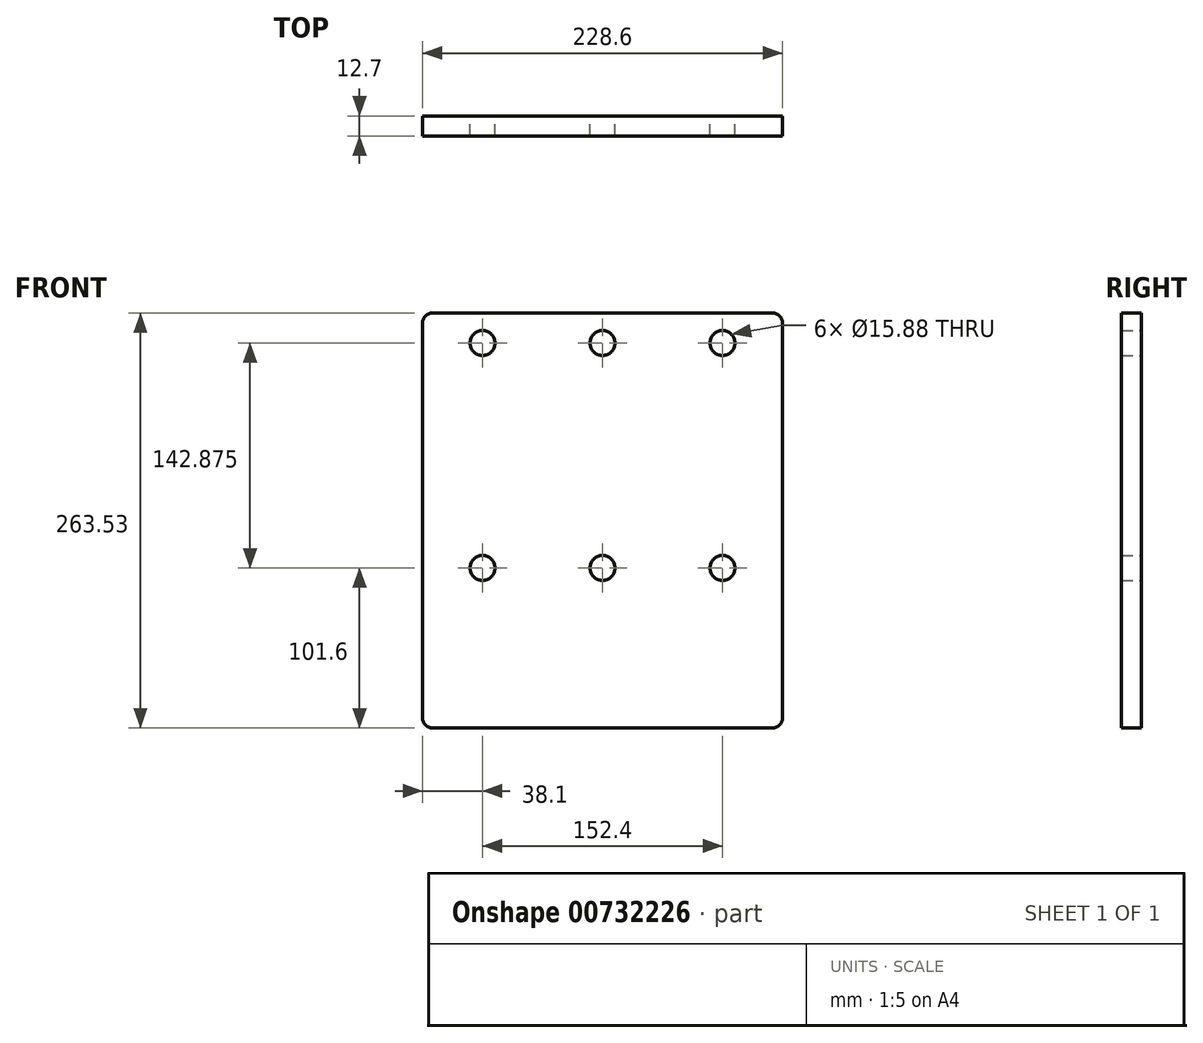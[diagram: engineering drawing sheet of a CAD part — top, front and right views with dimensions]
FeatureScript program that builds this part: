
annotation { "Feature Type Name" : "Feature", "Feature Type Description" : "" }
export const myFeature = defineFeature(function(context is Context, id is Id, definition is map)
    precondition{}
    {
        {
            var Q0;
            Q0=qCreatedBy(makeId("Front.planeOp"),FACE);
            var sketch = newSketch(context, id + "F0", { "sketchPlane" : qUnion([Q0])});
            skLineSegment(sketch, "E0.bottom", {"start": v(6.35, 0) * mm, "end": v(222.25, 0) * mm});
            skLineSegment(sketch, "E0.top", {"start": v(6.35, 263.53) * mm, "end": v(222.25, 263.53) * mm});
            skLineSegment(sketch, "E0.left", {"start": v(0, 6.35) * mm, "end": v(0, 257.18) * mm});
            skLineSegment(sketch, "E0.right", {"start": v(228.6, 6.35) * mm, "end": v(228.6, 257.18) * mm});
            skCircle(sketch, "E1", {"center": v(38.1, 101.6) * mm, "radius": 7.94 * mm});
            skCircle(sketch, "E2.0.1.0", {"center": v(38.1, 244.47) * mm, "radius": 7.94 * mm});
            skCircle(sketch, "E2.1.0.0", {"center": v(114.3, 101.6) * mm, "radius": 7.94 * mm});
            skCircle(sketch, "E2.1.1.0", {"center": v(114.3, 244.47) * mm, "radius": 7.94 * mm});
            skCircle(sketch, "E2.2.0.0", {"center": v(190.5, 101.6) * mm, "radius": 7.94 * mm});
            skCircle(sketch, "E2.2.1.0", {"center": v(190.5, 244.47) * mm, "radius": 7.94 * mm});
            skLineSegment(sketch, "E2.direction1", {"start": v(38.1, 101.6) * mm, "end": v(114.3, 101.6) * mm, "construction": true});
            skLineSegment(sketch, "E2.direction2", {"start": v(38.1, 101.6) * mm, "end": v(38.1, 244.47) * mm, "construction": true});
            skLineSegment(sketch, "E3", {"start": v(114.3, 263.53) * mm, "end": v(114.3, 0) * mm, "construction": true});
            skPoint(sketch, "E4.visualSharp", {"position": v(0, 263.53) * mm});
            skArc(sketch, "E4.filletArc", {"start": v(6.35, 263.53) * mm, "mid": v(1.86, 261.67) * mm, "end": v(0, 257.18) * mm});
            skPoint(sketch, "E5.visualSharp", {"position": v(228.6, 263.53) * mm});
            skArc(sketch, "E5.filletArc", {"start": v(228.6, 257.18) * mm, "mid": v(226.74, 261.67) * mm, "end": v(222.25, 263.53) * mm});
            skPoint(sketch, "E6.visualSharp", {"position": v(228.6, 0) * mm});
            skArc(sketch, "E6.filletArc", {"start": v(222.25, 0) * mm, "mid": v(226.74, 1.86) * mm, "end": v(228.6, 6.35) * mm});
            skPoint(sketch, "E7.visualSharp", {"position": v(0, 0) * mm});
            skArc(sketch, "E7.filletArc", {"start": v(0, 6.35) * mm, "mid": v(1.86, 1.86) * mm, "end": v(6.35, 0) * mm});
            skSolve(sketch);
        }
        {
            var Q0;
            Q0 = qSketchRegion(id + "F0", true);
            extrude(context, id + "F1", {"entities" : qUnion([Q0]), "depth" : 12.7 * mm, "offsetDistance" : 25.4 * mm});
        }
    });
